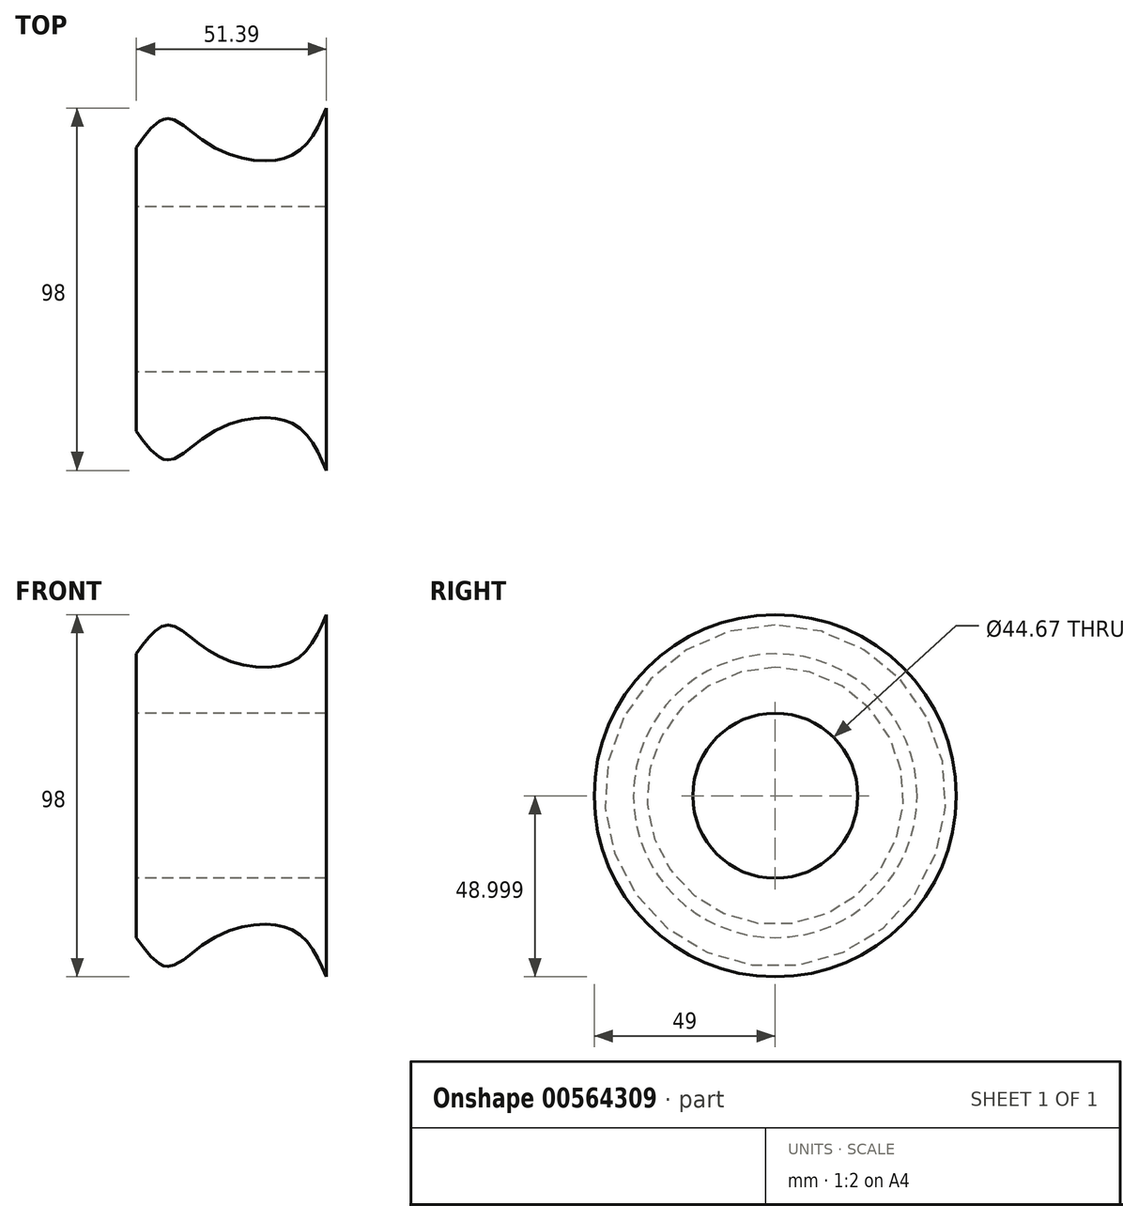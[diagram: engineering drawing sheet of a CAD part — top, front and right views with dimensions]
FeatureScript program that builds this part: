
annotation { "Feature Type Name" : "Feature", "Feature Type Description" : "" }
export const myFeature = defineFeature(function(context is Context, id is Id, definition is map)
    precondition{}
    {
        {
            var Q0;
            Q0=qCreatedBy(makeId("Front.planeOp"),FACE);
            var sketch = newSketch(context, id + "F0", { "sketchPlane" : qUnion([Q0])});
            skLineSegment(sketch, "E0", {"start": v(-76.54, 21.25) * mm, "end": v(62.88, 21.25) * mm});
            skLineSegment(sketch, "E1", {"start": v(-37.79, 59.63) * mm, "end": v(-37.79, 43.58) * mm});
            skLineSegment(sketch, "E2", {"start": v(-37.79, 43.58) * mm, "end": v(13.6, 43.58) * mm});
            skLineSegment(sketch, "E3", {"start": v(13.6, 43.58) * mm, "end": v(13.6, 70.25) * mm});
            skFitSpline(sketch, "E4", {"points": [v(-37.79, 59.63) * mm, v(-29.33, 67.43) * mm, v(-16.76, 59.63) * mm, v(4.28, 57.46) * mm, v(13.6, 70.25) * mm], "startDerivative": vector(38.2, 54.11) * mm, "endDerivative": vector(26.93, 62.4) * mm});
            skSolve(sketch);
        }
        {
            var Q0;
            Q0=makeQuery(id+"F0.imprint","IMPRINT",FACE,{"disambiguationData":[TD([[makeQuery(id+"F0.imprint","IMPRINT",EDGE,{"derivedFrom":sQuery(id+"F0.wireOp",EDGE,"E1")}),1.0]])]});
            var Q1;
            Q1=sQuery(id+"F0.wireOp",EDGE,"E0");
            revolve(context, id + "F1", {"entities" : qUnion([Q0]), "axis" : qUnion([Q1]), "revolveType" : RevolveType.FULL});
        }
    });
